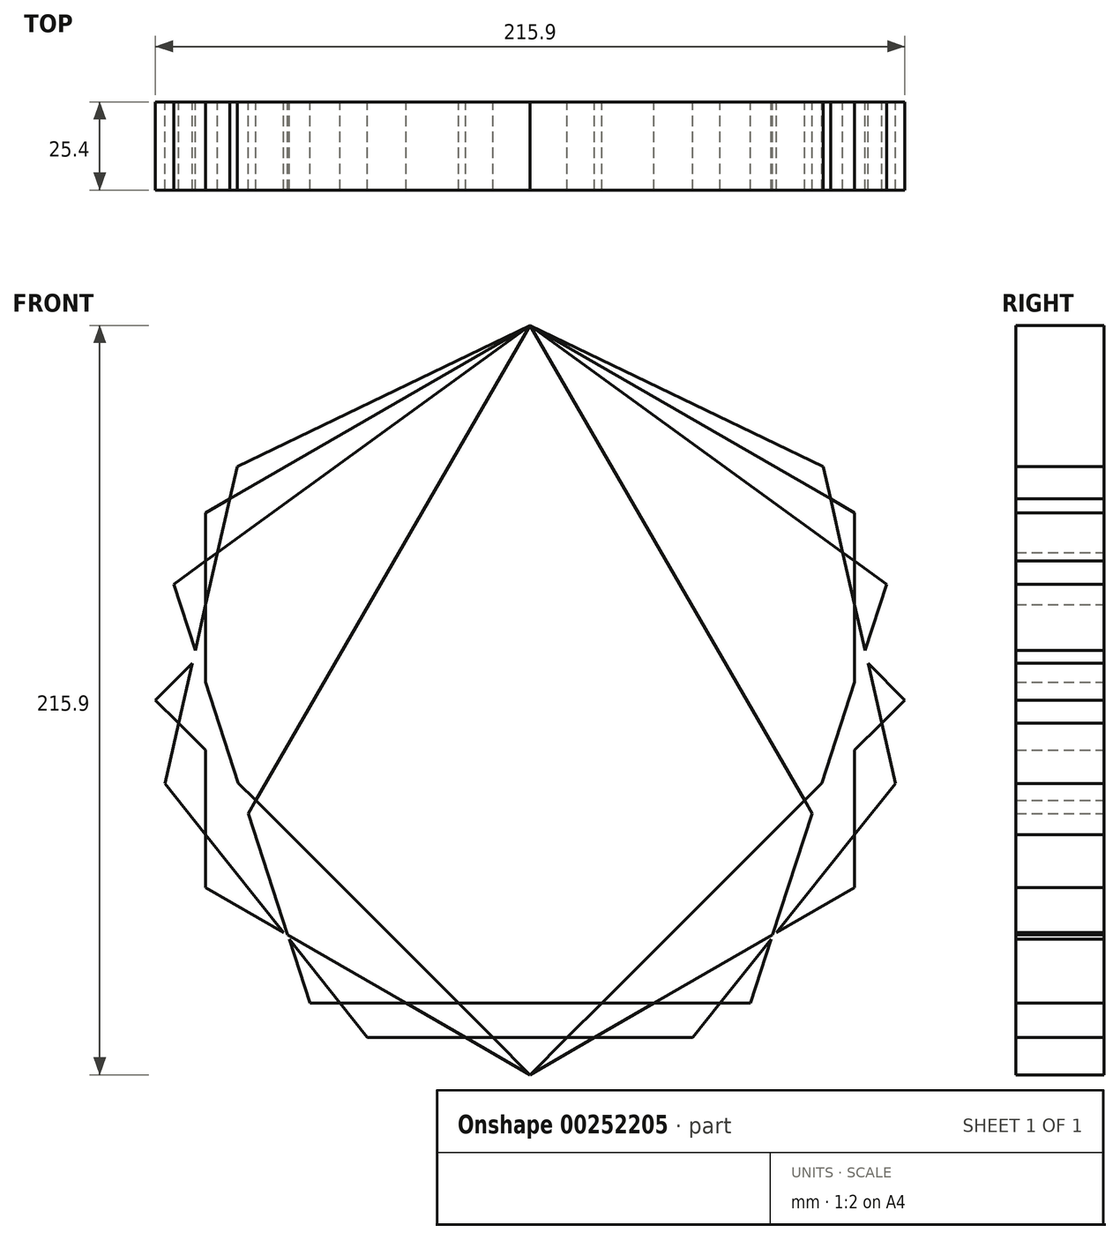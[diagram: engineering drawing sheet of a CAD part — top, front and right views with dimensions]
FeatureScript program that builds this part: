
annotation { "Feature Type Name" : "Feature", "Feature Type Description" : "" }
export const myFeature = defineFeature(function(context is Context, id is Id, definition is map)
    precondition{}
    {
        {
            var Q0;
            Q0=qCreatedBy(makeId("Front.planeOp"),FACE);
            var sketch = newSketch(context, id + "F0", { "sketchPlane" : qUnion([Q0])});
            skCircle(sketch, "E0", {"center": v(0, 0) * mm, "radius": 107.95 * mm});
            skCircle(sketch, "E1.cCircle", {"center": v(0, 0) * mm, "radius": 107.95 * mm, "construction": true});
            skLineSegment(sketch, "E1.0", {"start": v(0, 107.95) * mm, "end": v(84.4, 67.3) * mm});
            skLineSegment(sketch, "E1.1", {"start": v(84.4, 67.3) * mm, "end": v(105.24, -24.02) * mm});
            skLineSegment(sketch, "E1.2", {"start": v(105.24, -24.02) * mm, "end": v(46.84, -97.26) * mm});
            skLineSegment(sketch, "E1.3", {"start": v(46.84, -97.26) * mm, "end": v(-46.84, -97.26) * mm});
            skLineSegment(sketch, "E1.4", {"start": v(-46.84, -97.26) * mm, "end": v(-105.24, -24.02) * mm});
            skLineSegment(sketch, "E1.5", {"start": v(-105.24, -24.02) * mm, "end": v(-84.4, 67.3) * mm});
            skLineSegment(sketch, "E1.6", {"start": v(-84.4, 67.3) * mm, "end": v(0, 107.95) * mm});
            skLineSegment(sketch, "E2.0", {"start": v(0, 107.95) * mm, "end": v(93.49, 53.98) * mm});
            skLineSegment(sketch, "E2.1", {"start": v(93.49, 53.98) * mm, "end": v(93.49, -53.97) * mm});
            skLineSegment(sketch, "E2.2", {"start": v(93.49, -53.97) * mm, "end": v(0, -107.95) * mm});
            skLineSegment(sketch, "E2.3", {"start": v(0, -107.95) * mm, "end": v(-93.49, -53.98) * mm});
            skLineSegment(sketch, "E2.4", {"start": v(-93.49, -53.98) * mm, "end": v(-93.49, 53.97) * mm});
            skLineSegment(sketch, "E2.5", {"start": v(-93.49, 53.97) * mm, "end": v(0, 107.95) * mm});
            skLineSegment(sketch, "E3.0", {"start": v(0, 107.95) * mm, "end": v(102.67, 33.36) * mm});
            skLineSegment(sketch, "E3.1", {"start": v(102.67, 33.36) * mm, "end": v(63.45, -87.33) * mm});
            skLineSegment(sketch, "E3.2", {"start": v(63.45, -87.33) * mm, "end": v(-63.45, -87.33) * mm});
            skLineSegment(sketch, "E3.3", {"start": v(-63.45, -87.33) * mm, "end": v(-102.67, 33.36) * mm});
            skLineSegment(sketch, "E3.4", {"start": v(-102.67, 33.36) * mm, "end": v(0, 107.95) * mm});
            skLineSegment(sketch, "E4.0", {"start": v(0, 107.95) * mm, "end": v(107.95, 0) * mm});
            skLineSegment(sketch, "E4.1", {"start": v(107.95, 0) * mm, "end": v(0, -107.95) * mm});
            skLineSegment(sketch, "E4.2", {"start": v(0, -107.95) * mm, "end": v(-107.95, 0) * mm});
            skLineSegment(sketch, "E4.3", {"start": v(-107.95, 0) * mm, "end": v(0, 107.95) * mm});
            skLineSegment(sketch, "E5.0", {"start": v(0, 107.95) * mm, "end": v(93.49, -53.97) * mm});
            skLineSegment(sketch, "E5.1", {"start": v(93.49, -53.98) * mm, "end": v(-93.49, -53.98) * mm});
            skLineSegment(sketch, "E5.2", {"start": v(-93.49, -53.98) * mm, "end": v(0, 107.95) * mm});
            skSolve(sketch);
        }
        {
            var Q0;
            {var subQ0=sQuery(id+"F0.wireOp",EDGE,"E1.0");Q0=makeQuery(id+"F0.imprint","IMPRINT",FACE,{"disambiguationData":[TD([[makeQuery(id+"F0.imprint","IMPRINT",EDGE,{"derivedFrom":subQ0}),-1.0]])]});}
            var Q1;
            {var subQ0=sQuery(id+"F0.wireOp",EDGE,"E4.0");var subQ1=sQuery(id+"F0.wireOp",EDGE,"E1.1");var subQ2=makeQuery(id+"F0.imprint","INTERSECT",VERTEX,{"derivedFrom":[subQ1,subQ0]});Q1=makeQuery(id+"F0.imprint","IMPRINT",FACE,{"disambiguationData":[TD([[makeQuery(id+"F0.imprint","IMPRINT",EDGE,{"disambiguationData":[TD([[subQ2,-1.0]])],"derivedFrom":subQ1}),1.0]])]});}
            var Q2;
            {var subQ0=sQuery(id+"F0.wireOp",EDGE,"E2.1");var subQ1=sQuery(id+"F0.wireOp",EDGE,"E1.2");var subQ2=makeQuery(id+"F0.imprint","INTERSECT",VERTEX,{"derivedFrom":[subQ1,subQ0]});Q2=makeQuery(id+"F0.imprint","IMPRINT",FACE,{"disambiguationData":[TD([[makeQuery(id+"F0.imprint","IMPRINT",EDGE,{"disambiguationData":[TD([[subQ2,-1.0]])],"derivedFrom":subQ1}),1.0]])]});}
            var Q3;
            {var subQ0=sQuery(id+"F0.wireOp",EDGE,"E5.0");var subQ1=sQuery(id+"F0.wireOp",EDGE,"E1.2");var subQ2=makeQuery(id+"F0.imprint","INTERSECT",VERTEX,{"derivedFrom":[subQ1,subQ0]});Q3=makeQuery(id+"F0.imprint","IMPRINT",FACE,{"disambiguationData":[TD([[makeQuery(id+"F0.imprint","IMPRINT",EDGE,{"disambiguationData":[TD([[subQ2,-1.0]])],"derivedFrom":subQ1}),1.0]])]});}
            var Q4;
            {var subQ0=sQuery(id+"F0.wireOp",EDGE,"E5.1");var subQ1=sQuery(id+"F0.wireOp",EDGE,"E1.2");var subQ2=makeQuery(id+"F0.imprint","INTERSECT",VERTEX,{"derivedFrom":[subQ1,subQ0]});Q4=makeQuery(id+"F0.imprint","IMPRINT",FACE,{"disambiguationData":[TD([[makeQuery(id+"F0.imprint","IMPRINT",EDGE,{"disambiguationData":[TD([[subQ2,-1.0]])],"derivedFrom":subQ1}),1.0]])]});}
            var Q5;
            {var subQ0=sQuery(id+"F0.wireOp",EDGE,"E3.1");var subQ1=sQuery(id+"F0.wireOp",EDGE,"E1.2");var subQ2=makeQuery(id+"F0.imprint","INTERSECT",VERTEX,{"derivedFrom":[subQ1,subQ0]});Q5=makeQuery(id+"F0.imprint","IMPRINT",FACE,{"disambiguationData":[TD([[makeQuery(id+"F0.imprint","IMPRINT",EDGE,{"disambiguationData":[TD([[subQ2,-1.0]])],"derivedFrom":subQ1}),1.0]])]});}
            var Q6;
            {var subQ0=sQuery(id+"F0.wireOp",EDGE,"E2.2");var subQ1=sQuery(id+"F0.wireOp",EDGE,"E1.3");var subQ2=makeQuery(id+"F0.imprint","INTERSECT",VERTEX,{"derivedFrom":[subQ1,subQ0]});Q6=makeQuery(id+"F0.imprint","IMPRINT",FACE,{"disambiguationData":[TD([[makeQuery(id+"F0.imprint","IMPRINT",EDGE,{"disambiguationData":[TD([[subQ2,-1.0]])],"derivedFrom":subQ1}),1.0]])]});}
            var Q7;
            {var subQ0=sQuery(id+"F0.wireOp",EDGE,"E4.2");var subQ1=sQuery(id+"F0.wireOp",EDGE,"E1.3");var subQ2=makeQuery(id+"F0.imprint","INTERSECT",VERTEX,{"derivedFrom":[subQ1,subQ0]});Q7=makeQuery(id+"F0.imprint","IMPRINT",FACE,{"disambiguationData":[TD([[makeQuery(id+"F0.imprint","IMPRINT",EDGE,{"disambiguationData":[TD([[subQ2,-1.0]])],"derivedFrom":subQ1}),1.0]])]});}
            var Q8;
            {var subQ0=sQuery(id+"F0.wireOp",EDGE,"E3.2");var subQ1=sQuery(id+"F0.wireOp",EDGE,"E1.4");var subQ2=makeQuery(id+"F0.imprint","INTERSECT",VERTEX,{"derivedFrom":[subQ1,subQ0]});Q8=makeQuery(id+"F0.imprint","IMPRINT",FACE,{"disambiguationData":[TD([[makeQuery(id+"F0.imprint","IMPRINT",EDGE,{"disambiguationData":[TD([[subQ2,-1.0]])],"derivedFrom":subQ1}),1.0]])]});}
            var Q9;
            {var subQ0=sQuery(id+"F0.wireOp",EDGE,"E2.3");var subQ1=sQuery(id+"F0.wireOp",EDGE,"E1.4");var subQ2=makeQuery(id+"F0.imprint","INTERSECT",VERTEX,{"derivedFrom":[subQ1,subQ0]});Q9=makeQuery(id+"F0.imprint","IMPRINT",FACE,{"disambiguationData":[TD([[makeQuery(id+"F0.imprint","IMPRINT",EDGE,{"disambiguationData":[TD([[subQ2,-1.0]])],"derivedFrom":subQ1}),1.0]])]});}
            var Q10;
            {var subQ0=sQuery(id+"F0.wireOp",EDGE,"E5.1");var subQ1=sQuery(id+"F0.wireOp",EDGE,"E1.4");var subQ2=makeQuery(id+"F0.imprint","INTERSECT",VERTEX,{"derivedFrom":[subQ1,subQ0]});Q10=makeQuery(id+"F0.imprint","IMPRINT",FACE,{"disambiguationData":[TD([[makeQuery(id+"F0.imprint","IMPRINT",EDGE,{"disambiguationData":[TD([[subQ2,-1.0]])],"derivedFrom":subQ1}),1.0]])]});}
            var Q11;
            {var subQ0=sQuery(id+"F0.wireOp",EDGE,"E5.2");var subQ1=sQuery(id+"F0.wireOp",EDGE,"E1.4");var subQ2=makeQuery(id+"F0.imprint","INTERSECT",VERTEX,{"derivedFrom":[subQ1,subQ0]});Q11=makeQuery(id+"F0.imprint","IMPRINT",FACE,{"disambiguationData":[TD([[makeQuery(id+"F0.imprint","IMPRINT",EDGE,{"disambiguationData":[TD([[subQ2,-1.0]])],"derivedFrom":subQ1}),1.0]])]});}
            var Q12;
            {var subQ0=sQuery(id+"F0.wireOp",EDGE,"E4.2");var subQ1=sQuery(id+"F0.wireOp",EDGE,"E1.5");var subQ2=makeQuery(id+"F0.imprint","INTERSECT",VERTEX,{"derivedFrom":[subQ1,subQ0]});Q12=makeQuery(id+"F0.imprint","IMPRINT",FACE,{"disambiguationData":[TD([[makeQuery(id+"F0.imprint","IMPRINT",EDGE,{"disambiguationData":[TD([[subQ2,-1.0]])],"derivedFrom":subQ1}),1.0]])]});}
            var Q13;
            {var subQ0=sQuery(id+"F0.wireOp",EDGE,"E1.6");Q13=makeQuery(id+"F0.imprint","IMPRINT",FACE,{"disambiguationData":[TD([[makeQuery(id+"F0.imprint","IMPRINT",EDGE,{"derivedFrom":subQ0}),-1.0]])]});}
            var Q14;
            {var subQ0=sQuery(id+"F0.wireOp",EDGE,"E2.0");var subQ1=sQuery(id+"F0.wireOp",EDGE,"E1.1");var subQ2=makeQuery(id+"F0.imprint","INTERSECT",VERTEX,{"derivedFrom":[subQ1,subQ0]});Q14=makeQuery(id+"F0.imprint","IMPRINT",FACE,{"disambiguationData":[TD([[makeQuery(id+"F0.imprint","IMPRINT",EDGE,{"disambiguationData":[TD([[subQ2,-1.0]])],"derivedFrom":subQ1}),1.0]])]});}
            var Q15;
            {var subQ0=sQuery(id+"F0.wireOp",EDGE,"E3.0");var subQ1=sQuery(id+"F0.wireOp",EDGE,"E1.1");var subQ2=makeQuery(id+"F0.imprint","INTERSECT",VERTEX,{"derivedFrom":[subQ1,subQ0]});Q15=makeQuery(id+"F0.imprint","IMPRINT",FACE,{"disambiguationData":[TD([[makeQuery(id+"F0.imprint","IMPRINT",EDGE,{"disambiguationData":[TD([[subQ2,-1.0]])],"derivedFrom":subQ1}),-1.0]])]});}
            var Q16;
            {var subQ0=sQuery(id+"F0.wireOp",EDGE,"E2.1");var subQ1=sQuery(id+"F0.wireOp",EDGE,"E1.1");var subQ2=makeQuery(id+"F0.imprint","INTERSECT",VERTEX,{"derivedFrom":[subQ1,subQ0]});Q16=makeQuery(id+"F0.imprint","IMPRINT",FACE,{"disambiguationData":[TD([[makeQuery(id+"F0.imprint","IMPRINT",EDGE,{"disambiguationData":[TD([[subQ2,-1.0]])],"derivedFrom":subQ1}),1.0]])]});}
            var Q17;
            {var subQ0=sQuery(id+"F0.wireOp",EDGE,"E1.2");var subQ5=sQuery(id+"F0.wireOp",EDGE,"E2.1");var subQ6=makeQuery(id+"F0.imprint","INTERSECT",VERTEX,{"derivedFrom":[subQ0,subQ5]});Q17=makeQuery(id+"F0.imprint","IMPRINT",FACE,{"disambiguationData":[TD([[makeQuery(id+"F0.imprint","IMPRINT",EDGE,{"disambiguationData":[TD([[subQ6,1.0]])],"derivedFrom":subQ5}),1.0]])]});}
            var Q18;
            {var subQ0=sQuery(id+"F0.wireOp",EDGE,"E1.3");var subQ5=sQuery(id+"F0.wireOp",EDGE,"E2.2");var subQ6=makeQuery(id+"F0.imprint","INTERSECT",VERTEX,{"derivedFrom":[subQ0,subQ5]});Q18=makeQuery(id+"F0.imprint","IMPRINT",FACE,{"disambiguationData":[TD([[makeQuery(id+"F0.imprint","IMPRINT",EDGE,{"disambiguationData":[TD([[subQ6,1.0]])],"derivedFrom":subQ5}),1.0]])]});}
            var Q19;
            {var subQ1=sQuery(id+"F0.wireOp",EDGE,"E1.3");var subQ3=sQuery(id+"F0.wireOp",EDGE,"E2.3");var subQ4=makeQuery(id+"F0.imprint","INTERSECT",VERTEX,{"derivedFrom":[subQ1,subQ3]});Q19=makeQuery(id+"F0.imprint","IMPRINT",FACE,{"disambiguationData":[TD([[makeQuery(id+"F0.imprint","IMPRINT",EDGE,{"disambiguationData":[TD([[subQ4,-1.0]])],"derivedFrom":subQ3}),1.0]])]});}
            var Q20;
            {var subQ1=sQuery(id+"F0.wireOp",EDGE,"E1.4");var subQ3=sQuery(id+"F0.wireOp",EDGE,"E2.4");var subQ4=makeQuery(id+"F0.imprint","INTERSECT",VERTEX,{"derivedFrom":[subQ1,subQ3]});Q20=makeQuery(id+"F0.imprint","IMPRINT",FACE,{"disambiguationData":[TD([[makeQuery(id+"F0.imprint","IMPRINT",EDGE,{"disambiguationData":[TD([[subQ4,-1.0]])],"derivedFrom":subQ3}),1.0]])]});}
            var Q21;
            {var subQ0=sQuery(id+"F0.wireOp",EDGE,"E3.3");var subQ1=sQuery(id+"F0.wireOp",EDGE,"E1.5");var subQ2=makeQuery(id+"F0.imprint","INTERSECT",VERTEX,{"derivedFrom":[subQ1,subQ0]});Q21=makeQuery(id+"F0.imprint","IMPRINT",FACE,{"disambiguationData":[TD([[makeQuery(id+"F0.imprint","IMPRINT",EDGE,{"disambiguationData":[TD([[subQ2,-1.0]])],"derivedFrom":subQ1}),1.0]])]});}
            var Q22;
            {var subQ0=sQuery(id+"F0.wireOp",EDGE,"E2.4");var subQ1=sQuery(id+"F0.wireOp",EDGE,"E1.5");var subQ2=makeQuery(id+"F0.imprint","INTERSECT",VERTEX,{"derivedFrom":[subQ1,subQ0]});Q22=makeQuery(id+"F0.imprint","IMPRINT",FACE,{"disambiguationData":[TD([[makeQuery(id+"F0.imprint","IMPRINT",EDGE,{"disambiguationData":[TD([[subQ2,-1.0]])],"derivedFrom":subQ1}),-1.0]])]});}
            var Q23;
            {var subQ0=sQuery(id+"F0.wireOp",EDGE,"E3.4");var subQ1=sQuery(id+"F0.wireOp",EDGE,"E1.5");var subQ2=makeQuery(id+"F0.imprint","INTERSECT",VERTEX,{"derivedFrom":[subQ1,subQ0]});Q23=makeQuery(id+"F0.imprint","IMPRINT",FACE,{"disambiguationData":[TD([[makeQuery(id+"F0.imprint","IMPRINT",EDGE,{"disambiguationData":[TD([[subQ2,-1.0]])],"derivedFrom":subQ1}),1.0]])]});}
            var Q24;
            {var subQ5=sQuery(id+"F0.wireOp",EDGE,"E4.0");var subQ7=sQuery(id+"F0.wireOp",EDGE,"E2.1");var subQ8=makeQuery(id+"F0.imprint","INTERSECT",VERTEX,{"derivedFrom":[subQ7,subQ5]});Q24=makeQuery(id+"F0.imprint","IMPRINT",FACE,{"disambiguationData":[TD([[makeQuery(id+"F0.imprint","IMPRINT",EDGE,{"disambiguationData":[TD([[subQ8,-1.0]])],"derivedFrom":subQ7}),-1.0]])]});}
            var Q25;
            {var subQ3=sQuery(id+"F0.wireOp",EDGE,"E2.4");var subQ6=sQuery(id+"F0.wireOp",EDGE,"E3.3");var subQ9=makeQuery(id+"F0.imprint","INTERSECT",VERTEX,{"derivedFrom":[subQ3,subQ6]});Q25=makeQuery(id+"F0.imprint","IMPRINT",FACE,{"disambiguationData":[TD([[makeQuery(id+"F0.imprint","IMPRINT",EDGE,{"disambiguationData":[TD([[subQ9,-1.0]])],"derivedFrom":subQ3}),-1.0]])]});}
            var Q26;
            {var subQ0=sQuery(id+"F0.wireOp",EDGE,"E5.1");var subQ1=sQuery(id+"F0.wireOp",EDGE,"E3.3");var subQ2=makeQuery(id+"F0.imprint","INTERSECT",VERTEX,{"derivedFrom":[subQ1,subQ0]});Q26=makeQuery(id+"F0.imprint","IMPRINT",FACE,{"disambiguationData":[TD([[makeQuery(id+"F0.imprint","IMPRINT",EDGE,{"disambiguationData":[TD([[subQ2,-1.0]])],"derivedFrom":subQ1}),-1.0]])]});}
            var Q27;
            {var subQ5=sQuery(id+"F0.wireOp",EDGE,"E2.2");var subQ7=sQuery(id+"F0.wireOp",EDGE,"E3.1");var subQ8=makeQuery(id+"F0.imprint","INTERSECT",VERTEX,{"derivedFrom":[subQ5,subQ7]});Q27=makeQuery(id+"F0.imprint","IMPRINT",FACE,{"disambiguationData":[TD([[makeQuery(id+"F0.imprint","IMPRINT",EDGE,{"disambiguationData":[TD([[subQ8,-1.0]])],"derivedFrom":subQ5}),-1.0]])]});}
            var Q28;
            {var subQ1=sQuery(id+"F0.wireOp",EDGE,"E3.2");var subQ6=sQuery(id+"F0.wireOp",EDGE,"E2.3");var subQ9=makeQuery(id+"F0.imprint","INTERSECT",VERTEX,{"derivedFrom":[subQ6,subQ1]});Q28=makeQuery(id+"F0.imprint","IMPRINT",FACE,{"disambiguationData":[TD([[makeQuery(id+"F0.imprint","IMPRINT",EDGE,{"disambiguationData":[TD([[subQ9,-1.0]])],"derivedFrom":subQ6}),-1.0]])]});}
            var Q29;
            {var subQ0=sQuery(id+"F0.wireOp",EDGE,"E4.1");var subQ1=sQuery(id+"F0.wireOp",EDGE,"E1.3");var subQ2=makeQuery(id+"F0.imprint","INTERSECT",VERTEX,{"derivedFrom":[subQ1,subQ0]});Q29=makeQuery(id+"F0.imprint","IMPRINT",FACE,{"disambiguationData":[TD([[makeQuery(id+"F0.imprint","IMPRINT",EDGE,{"disambiguationData":[TD([[subQ2,-1.0]])],"derivedFrom":subQ1}),-1.0]])]});}
            var Q30;
            {var subQ0=sQuery(id+"F0.wireOp",EDGE,"E5.0");var subQ1=sQuery(id+"F0.wireOp",EDGE,"E3.1");var subQ2=makeQuery(id+"F0.imprint","INTERSECT",VERTEX,{"derivedFrom":[subQ1,subQ0]});Q30=makeQuery(id+"F0.imprint","IMPRINT",FACE,{"disambiguationData":[TD([[makeQuery(id+"F0.imprint","IMPRINT",EDGE,{"disambiguationData":[TD([[subQ2,-1.0]])],"derivedFrom":subQ1}),-1.0]])]});}
            extrude(context, id + "F1", {"entities" : qUnion([Q0, Q1, Q2, Q3, Q4, Q5, Q6, Q7, Q8, Q9, Q10, Q11, Q12, Q13, Q14, Q15, Q16, Q17, Q18, Q19, Q20, Q21, Q22, Q23, Q24, Q25, Q26, Q27, Q28, Q29, Q30]), "depth" : 25.4 * mm});
        }
    });
